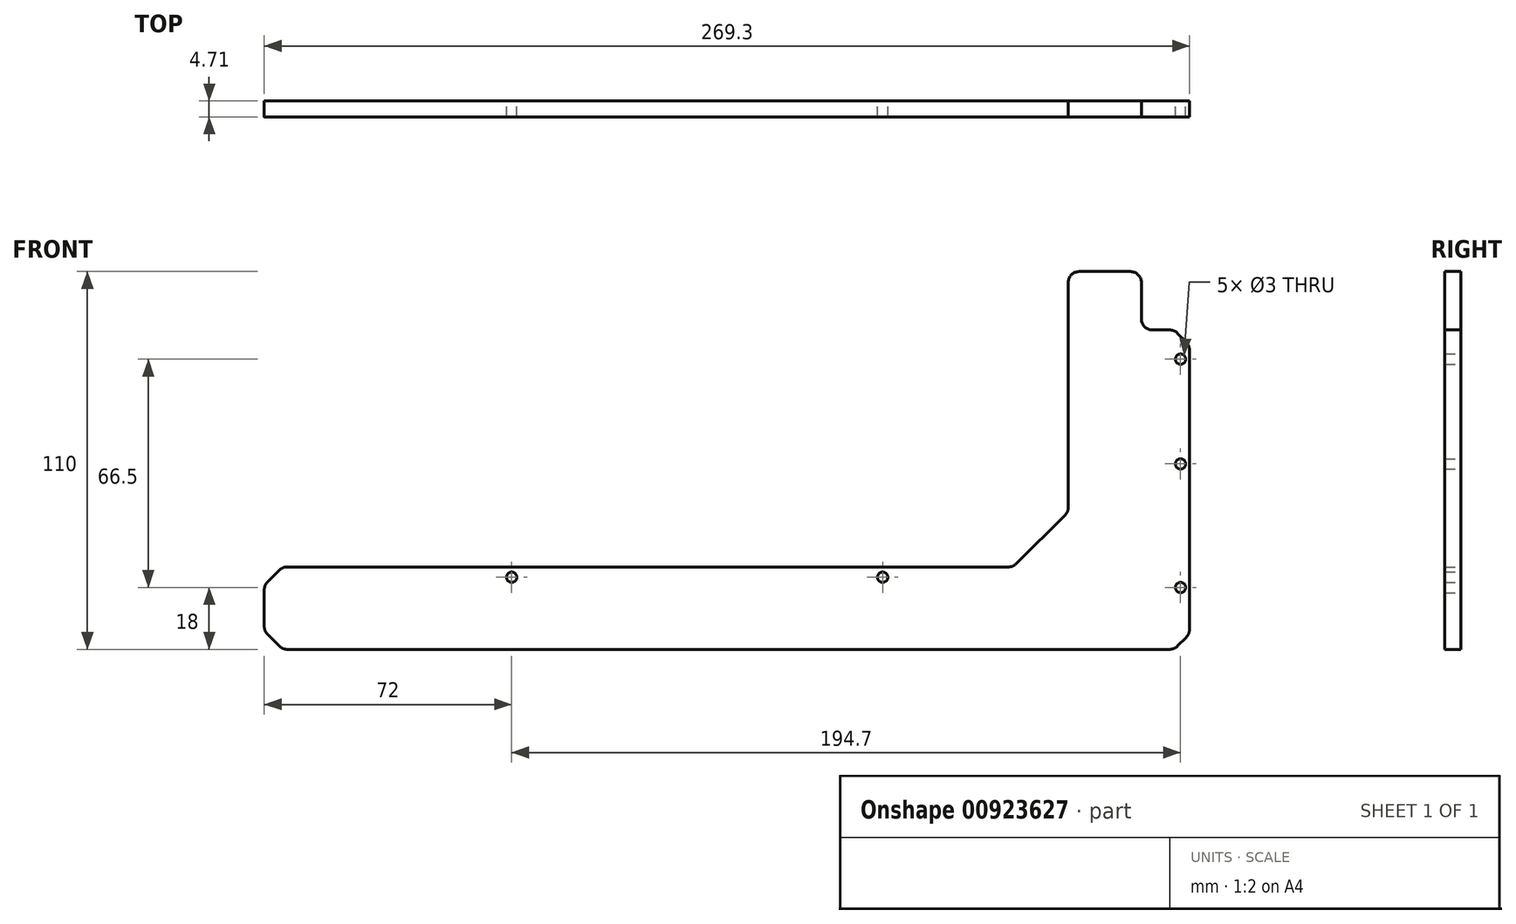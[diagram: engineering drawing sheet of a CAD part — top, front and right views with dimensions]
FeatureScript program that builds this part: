
annotation { "Feature Type Name" : "Feature", "Feature Type Description" : "" }
export const myFeature = defineFeature(function(context is Context, id is Id, definition is map)
    precondition{}
    {
        {
            var Q0;
            Q0=qCreatedBy(makeId("Front.planeOp"),FACE);
            var sketch = newSketch(context, id + "F0", { "sketchPlane" : qUnion([Q0])});
            skLineSegment(sketch, "E0.bottom", {"start": v(0, 0) * mm, "end": v(-255.3, 0) * mm});
            skLineSegment(sketch, "E0.top", {"start": v(-21.3, 24) * mm, "end": v(-255.3, 24) * mm, "construction": true});
            skLineSegment(sketch, "E0.right", {"start": v(-255.3, 0) * mm, "end": v(-255.3, 24) * mm, "construction": true});
            skLineSegment(sketch, "E1.top", {"start": v(-21.3, 110) * mm, "end": v(0, 110) * mm, "construction": true});
            skLineSegment(sketch, "E1.left", {"start": v(-21.3, 24) * mm, "end": v(-21.3, 110) * mm, "construction": true});
            skLineSegment(sketch, "E1.right", {"start": v(0, 0) * mm, "end": v(0, 110) * mm, "construction": true});
            skLineSegment(sketch, "E2", {"start": v(-37.3, 24) * mm, "end": v(-21.3, 40) * mm, "construction": true});
            skLineSegment(sketch, "E3", {"start": v(0, 0) * mm, "end": v(9.58, 0) * mm, "construction": true});
            skLineSegment(sketch, "E4", {"start": v(9.58, 0) * mm, "end": v(14, 4.42) * mm, "construction": true});
            skLineSegment(sketch, "E5", {"start": v(14, 88.58) * mm, "end": v(14, 4.42) * mm, "construction": true});
            skLineSegment(sketch, "E6", {"start": v(14, 88.58) * mm, "end": v(9.58, 93) * mm, "construction": true});
            skLineSegment(sketch, "E7", {"start": v(9.58, 93) * mm, "end": v(0, 93) * mm, "construction": true});
            skLineSegment(sketch, "E8.bottom", {"start": v(4.8, 75.5) * mm, "end": v(11, 75.5) * mm, "construction": true});
            skLineSegment(sketch, "E8.top", {"start": v(4.8, 68.5) * mm, "end": v(11, 68.5) * mm, "construction": true});
            skLineSegment(sketch, "E8.left", {"start": v(4.8, 75.5) * mm, "end": v(4.8, 68.5) * mm, "construction": true});
            skLineSegment(sketch, "E8.right", {"start": v(11, 75.5) * mm, "end": v(11, 68.5) * mm, "construction": true});
            skLineSegment(sketch, "E9.bottom", {"start": v(11, 32.5) * mm, "end": v(4.8, 32.5) * mm, "construction": true});
            skLineSegment(sketch, "E9.top", {"start": v(11, 39.5) * mm, "end": v(4.8, 39.5) * mm, "construction": true});
            skLineSegment(sketch, "E9.left", {"start": v(11, 32.5) * mm, "end": v(11, 39.5) * mm, "construction": true});
            skLineSegment(sketch, "E9.right", {"start": v(4.8, 32.5) * mm, "end": v(4.8, 39.5) * mm, "construction": true});
            skCircle(sketch, "E10", {"center": v(-183.3, 21) * mm, "radius": 1.5 * mm, "construction": true});
            skCircle(sketch, "E11", {"center": v(-75.3, 21) * mm, "radius": 1.5 * mm, "construction": true});
            skLineSegment(sketch, "E12.bottom", {"start": v(-222.8, 22.5) * mm, "end": v(-215.8, 22.5) * mm, "construction": true});
            skLineSegment(sketch, "E12.top", {"start": v(-222.8, 16.1) * mm, "end": v(-215.8, 16.1) * mm, "construction": true});
            skLineSegment(sketch, "E12.left", {"start": v(-222.8, 22.5) * mm, "end": v(-222.8, 16.1) * mm, "construction": true});
            skLineSegment(sketch, "E12.right", {"start": v(-215.8, 22.5) * mm, "end": v(-215.8, 16.1) * mm, "construction": true});
            skLineSegment(sketch, "E13.bottom", {"start": v(-150.8, 22.5) * mm, "end": v(-143.8, 22.5) * mm, "construction": true});
            skLineSegment(sketch, "E13.top", {"start": v(-150.8, 16.1) * mm, "end": v(-143.8, 16.1) * mm, "construction": true});
            skLineSegment(sketch, "E13.left", {"start": v(-150.8, 22.5) * mm, "end": v(-150.8, 16.1) * mm, "construction": true});
            skLineSegment(sketch, "E13.right", {"start": v(-143.8, 22.5) * mm, "end": v(-143.8, 16.1) * mm, "construction": true});
            skLineSegment(sketch, "E14.bottom", {"start": v(-114.8, 22.5) * mm, "end": v(-107.8, 22.5) * mm, "construction": true});
            skLineSegment(sketch, "E14.top", {"start": v(-114.8, 16.1) * mm, "end": v(-107.8, 16.1) * mm, "construction": true});
            skLineSegment(sketch, "E14.left", {"start": v(-114.8, 22.5) * mm, "end": v(-114.8, 16.1) * mm, "construction": true});
            skLineSegment(sketch, "E14.right", {"start": v(-107.8, 22.5) * mm, "end": v(-107.8, 16.1) * mm, "construction": true});
            skLineSegment(sketch, "E15.bottom", {"start": v(-42.8, 22.5) * mm, "end": v(-35.8, 22.5) * mm, "construction": true});
            skLineSegment(sketch, "E15.top", {"start": v(-42.8, 16.1) * mm, "end": v(-35.8, 16.1) * mm, "construction": true});
            skLineSegment(sketch, "E15.left", {"start": v(-42.8, 22.5) * mm, "end": v(-42.8, 16.1) * mm, "construction": true});
            skLineSegment(sketch, "E15.right", {"start": v(-35.8, 22.5) * mm, "end": v(-35.8, 16.1) * mm, "construction": true});
            skLineSegment(sketch, "E16", {"start": v(-255.3, 18.7) * mm, "end": v(-250, 24) * mm, "construction": true});
            skLineSegment(sketch, "E17", {"start": v(-255.3, 5.3) * mm, "end": v(-250, 0) * mm, "construction": true});
            skLineSegment(sketch, "E18", {"start": v(-244.85, 5.9) * mm, "end": v(-237.77, 12.97) * mm, "construction": true});
            skLineSegment(sketch, "E19", {"start": v(-237.77, 12.97) * mm, "end": v(-242.3, 17.5) * mm, "construction": true});
            skLineSegment(sketch, "E20", {"start": v(-242.3, 17.5) * mm, "end": v(-249.37, 10.43) * mm, "construction": true});
            skLineSegment(sketch, "E21", {"start": v(-249.37, 10.43) * mm, "end": v(-244.85, 5.9) * mm, "construction": true});
            skCircle(sketch, "E22", {"center": v(11.4, 84.5) * mm, "radius": 1.5 * mm});
            skCircle(sketch, "E23", {"center": v(11.4, 54) * mm, "radius": 1.5 * mm});
            skCircle(sketch, "E24", {"center": v(11.4, 18) * mm, "radius": 1.5 * mm});
            skLineSegment(sketch, "E25", {"start": v(-21.3, 24) * mm, "end": v(-39.3, 0) * mm, "construction": true});
            skPoint(sketch, "E25.endSnap0", {"position": v(-39.3, 16.1) * mm});
            skLineSegment(sketch, "E26", {"start": v(-39.3, 0) * mm, "end": v(-57.3, 24) * mm, "construction": true});
            skLineSegment(sketch, "E27", {"start": v(-57.3, 24) * mm, "end": v(-75.3, 0) * mm, "construction": true});
            skLineSegment(sketch, "E28", {"start": v(-75.3, 0) * mm, "end": v(-93.3, 24) * mm, "construction": true});
            skLineSegment(sketch, "E29", {"start": v(-93.3, 24) * mm, "end": v(-111.3, 0) * mm, "construction": true});
            skPoint(sketch, "E29.endSnap0", {"position": v(-111.3, 16.1) * mm});
            skLineSegment(sketch, "E30", {"start": v(-111.3, 0) * mm, "end": v(-129.3, 24) * mm, "construction": true});
            skLineSegment(sketch, "E31", {"start": v(-129.3, 24) * mm, "end": v(-147.3, 0) * mm, "construction": true});
            skPoint(sketch, "E31.endSnap0", {"position": v(-147.3, 16.1) * mm});
            skLineSegment(sketch, "E32", {"start": v(-147.3, 0) * mm, "end": v(-165.3, 24) * mm, "construction": true});
            skLineSegment(sketch, "E33", {"start": v(-165.3, 24) * mm, "end": v(-183.3, 0) * mm, "construction": true});
            skLineSegment(sketch, "E34", {"start": v(-183.3, 0) * mm, "end": v(-201.3, 24) * mm, "construction": true});
            skLineSegment(sketch, "E35", {"start": v(-201.3, 24) * mm, "end": v(-219.3, 0) * mm, "construction": true});
            skPoint(sketch, "E35.endSnap0", {"position": v(-219.3, 16.1) * mm});
            skLineSegment(sketch, "E36", {"start": v(-219.3, 0) * mm, "end": v(-237.3, 24) * mm, "construction": true});
            skLineSegment(sketch, "E37", {"start": v(-75.3, 21) * mm, "end": v(-39.3, 21) * mm, "construction": true});
            skPoint(sketch, "E38", {"position": v(-57.3, 21) * mm});
            skLineSegment(sketch, "E39", {"start": v(-111.3, 21) * mm, "end": v(-75.3, 21) * mm, "construction": true});
            skLineSegment(sketch, "E40", {"start": v(-147.3, 21) * mm, "end": v(-111.3, 21) * mm, "construction": true});
            skLineSegment(sketch, "E41", {"start": v(-183.3, 21) * mm, "end": v(-147.3, 21) * mm, "construction": true});
            skLineSegment(sketch, "E42", {"start": v(-219.3, 21) * mm, "end": v(-183.3, 21) * mm, "construction": true});
            skPoint(sketch, "E43", {"position": v(-93.3, 21) * mm});
            skPoint(sketch, "E44", {"position": v(-129.3, 21) * mm});
            skPoint(sketch, "E45", {"position": v(-165.3, 21) * mm});
            skPoint(sketch, "E46", {"position": v(-201.3, 21) * mm});
            skLineSegment(sketch, "E47", {"start": v(4.8, 72) * mm, "end": v(-21.3, 72) * mm, "construction": true});
            skLineSegment(sketch, "E48", {"start": v(4.8, 36) * mm, "end": v(-21.3, 36) * mm, "construction": true});
            skLineSegment(sketch, "E49", {"start": v(-219.3, 21) * mm, "end": v(-255.3, 21) * mm, "construction": true});
            skPoint(sketch, "E50", {"position": v(-237.3, 21) * mm});
            skSolve(sketch);
        }
        {
            var Q0;
            Q0=qCreatedBy(makeId("Front.planeOp"),FACE);
            var sketch = newSketch(context, id + "F1", { "sketchPlane" : qUnion([Q0])});
            skLineSegment(sketch, "E51", {"start": v(-250, 24) * mm, "end": v(-255.3, 18.7) * mm});
            skLineSegment(sketch, "E52", {"start": v(-255.3, 18.7) * mm, "end": v(-255.3, 5.3) * mm});
            skLineSegment(sketch, "E53", {"start": v(-255.3, 5.3) * mm, "end": v(-250, 0) * mm});
            skLineSegment(sketch, "E54", {"start": v(-250, 0) * mm, "end": v(9.58, 0) * mm});
            skLineSegment(sketch, "E55", {"start": v(9.58, 0) * mm, "end": v(14, 4.42) * mm});
            skLineSegment(sketch, "E56", {"start": v(14, 4.42) * mm, "end": v(14, 88.58) * mm});
            skLineSegment(sketch, "E57", {"start": v(14, 88.58) * mm, "end": v(9.58, 93) * mm});
            skLineSegment(sketch, "E58", {"start": v(9.58, 93) * mm, "end": v(0, 93) * mm});
            skLineSegment(sketch, "E59", {"start": v(0, 93) * mm, "end": v(0, 110) * mm});
            skLineSegment(sketch, "E60", {"start": v(0, 110) * mm, "end": v(-21.3, 110) * mm});
            skLineSegment(sketch, "E61", {"start": v(-21.3, 110) * mm, "end": v(-21.3, 40) * mm});
            skLineSegment(sketch, "E62", {"start": v(-21.3, 40) * mm, "end": v(-37.3, 24) * mm});
            skLineSegment(sketch, "E63", {"start": v(-37.3, 24) * mm, "end": v(-250, 24) * mm});
            skCircle(sketch, "E64", {"center": v(11.4, 84.5) * mm, "radius": 1.5 * mm});
            skCircle(sketch, "E65", {"center": v(11.4, 54) * mm, "radius": 1.5 * mm});
            skCircle(sketch, "E66", {"center": v(11.4, 18) * mm, "radius": 1.5 * mm});
            skCircle(sketch, "E67", {"center": v(-75.3, 21) * mm, "radius": 1.5 * mm});
            skCircle(sketch, "E68", {"center": v(-183.3, 21) * mm, "radius": 1.5 * mm});
            skSolve(sketch);
        }
        {
            var Q0;
            Q0 = qSketchRegion(id + "F1", true);
            extrude(context, id + "F2", {"entities" : qUnion([Q0]), "depth" : 2.35 * mm, "offsetDistance" : 25.4 * mm, "hasSecondDirection" : true, "secondDirectionOppositeDirection" : true, "secondDirectionDepth" : 2.36 * mm});
        }
        {
            var Q0;
            Q0=makeQuery(id+"F2.opExtrude","SWEPT_EDGE",EDGE,{"disambiguationData":[OSD([sQuery(id+"F1.wireOp",EDGE,"E51"),sQuery(id+"F1.wireOp",EDGE,"E63")])]});
            var Q1;
            Q1=makeQuery(id+"F2.opExtrude","SWEPT_EDGE",EDGE,{"disambiguationData":[OSD([sQuery(id+"F1.wireOp",EDGE,"E51"),sQuery(id+"F1.wireOp",EDGE,"E52")])]});
            var Q2;
            Q2=makeQuery(id+"F2.opExtrude","SWEPT_EDGE",EDGE,{"disambiguationData":[OSD([sQuery(id+"F1.wireOp",EDGE,"E52"),sQuery(id+"F1.wireOp",EDGE,"E53")])]});
            var Q3;
            Q3=makeQuery(id+"F2.opExtrude","SWEPT_EDGE",EDGE,{"disambiguationData":[OSD([sQuery(id+"F1.wireOp",EDGE,"E53"),sQuery(id+"F1.wireOp",EDGE,"E54")])]});
            var Q4;
            Q4=makeQuery(id+"F2.opExtrude","SWEPT_EDGE",EDGE,{"disambiguationData":[OSD([sQuery(id+"F1.wireOp",EDGE,"E54"),sQuery(id+"F1.wireOp",EDGE,"E55")])]});
            var Q5;
            Q5=makeQuery(id+"F2.opExtrude","SWEPT_EDGE",EDGE,{"disambiguationData":[OSD([sQuery(id+"F1.wireOp",EDGE,"E55"),sQuery(id+"F1.wireOp",EDGE,"E56")])]});
            var Q6;
            Q6=makeQuery(id+"F2.opExtrude","SWEPT_EDGE",EDGE,{"disambiguationData":[OSD([sQuery(id+"F1.wireOp",EDGE,"E56"),sQuery(id+"F1.wireOp",EDGE,"E57")])]});
            var Q7;
            Q7=makeQuery(id+"F2.opExtrude","SWEPT_EDGE",EDGE,{"disambiguationData":[OSD([sQuery(id+"F1.wireOp",EDGE,"E57"),sQuery(id+"F1.wireOp",EDGE,"E58")])]});
            var Q8;
            Q8=makeQuery(id+"F2.opExtrude","SWEPT_EDGE",EDGE,{"disambiguationData":[OSD([sQuery(id+"F1.wireOp",EDGE,"E58"),sQuery(id+"F1.wireOp",EDGE,"E59")])]});
            var Q9;
            Q9=makeQuery(id+"F2.opExtrude","SWEPT_EDGE",EDGE,{"disambiguationData":[OSD([sQuery(id+"F1.wireOp",EDGE,"E59"),sQuery(id+"F1.wireOp",EDGE,"E60")])]});
            var Q10;
            Q10=makeQuery(id+"F2.opExtrude","SWEPT_EDGE",EDGE,{"disambiguationData":[OSD([sQuery(id+"F1.wireOp",EDGE,"E60"),sQuery(id+"F1.wireOp",EDGE,"E61")])]});
            var Q11;
            Q11=makeQuery(id+"F2.opExtrude","SWEPT_EDGE",EDGE,{"disambiguationData":[OSD([sQuery(id+"F1.wireOp",EDGE,"E61"),sQuery(id+"F1.wireOp",EDGE,"E62")])]});
            var Q12;
            Q12=makeQuery(id+"F2.opExtrude","SWEPT_EDGE",EDGE,{"disambiguationData":[OSD([sQuery(id+"F1.wireOp",EDGE,"E62"),sQuery(id+"F1.wireOp",EDGE,"E63")])]});
            fillet(context, id + "F3", {"entities" : qUnion([Q0, Q1, Q2, Q3, Q4, Q5, Q6, Q7, Q8, Q9, Q10, Q11, Q12]), "radius" : 3.17 * mm, "tangentPropagation" : true, "allowEdgeOverflow" : false});
        }
    });
